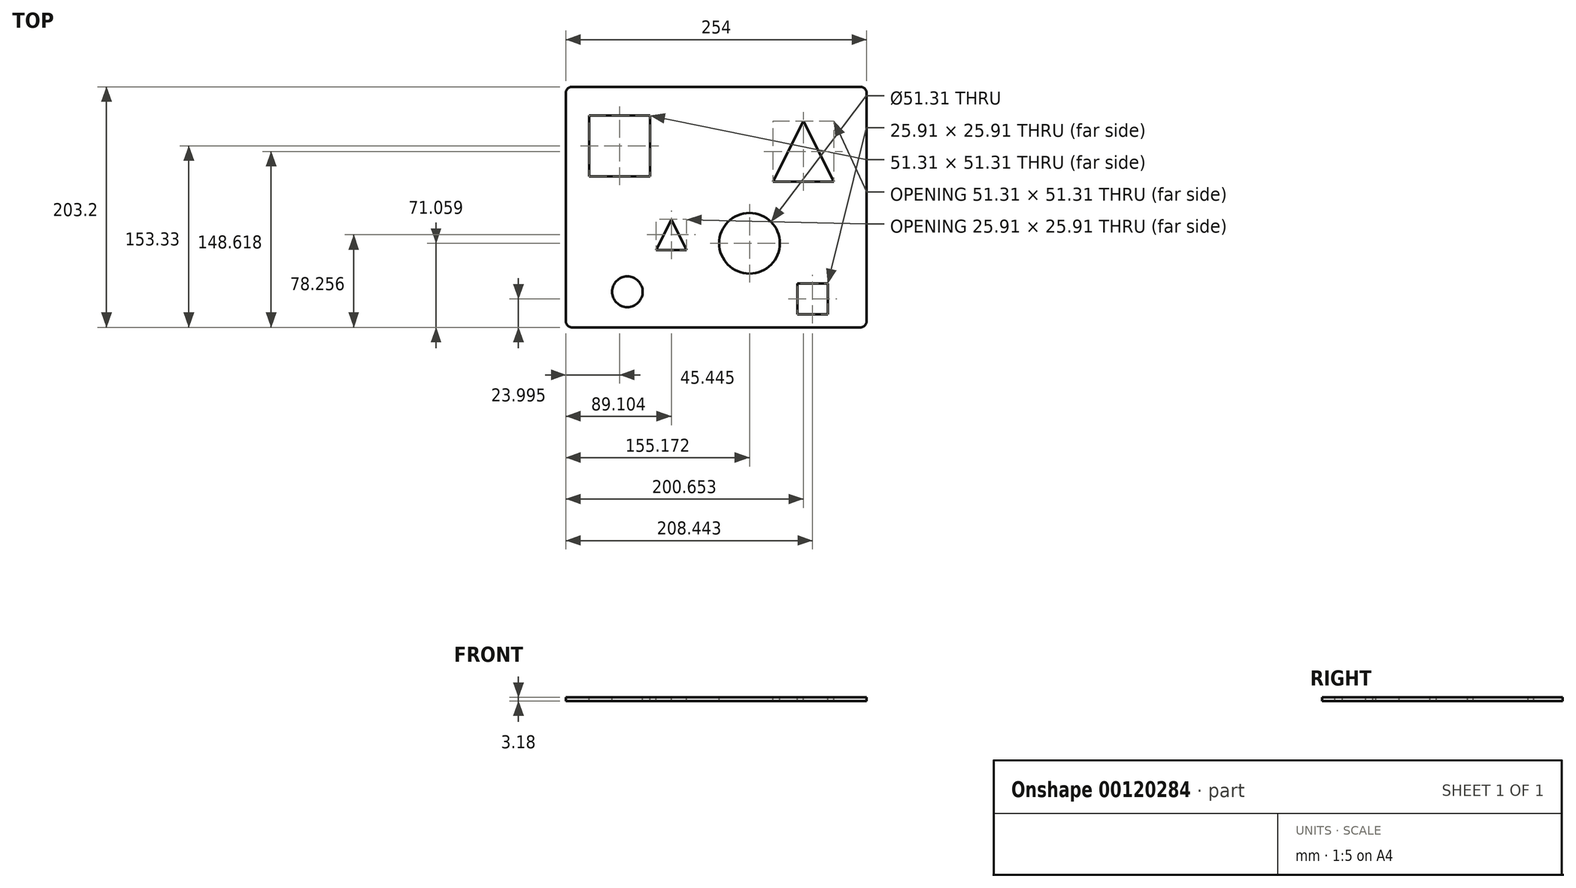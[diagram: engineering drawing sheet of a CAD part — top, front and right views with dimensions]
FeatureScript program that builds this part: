
annotation { "Feature Type Name" : "Feature", "Feature Type Description" : "" }
export const myFeature = defineFeature(function(context is Context, id is Id, definition is map)
    precondition{}
    {
        {
            var Q0;
            Q0=qCreatedBy(makeId("Top.planeOp"),FACE);
            var sketch = newSketch(context, id + "F0", { "sketchPlane" : qUnion([Q0])});
            skLineSegment(sketch, "E0.bottom", {"start": v(-123.95, 112) * mm, "end": v(130.05, 112) * mm});
            skLineSegment(sketch, "E0.top", {"start": v(-123.95, -91.2) * mm, "end": v(130.05, -91.2) * mm});
            skLineSegment(sketch, "E0.left", {"start": v(-123.95, 112) * mm, "end": v(-123.95, -91.2) * mm});
            skLineSegment(sketch, "E0.right", {"start": v(130.05, 112) * mm, "end": v(130.05, -91.2) * mm});
            skSolve(sketch);
        }
        {
            var Q0;
            Q0 = qSketchRegion(id + "F0", true);
            extrude(context, id + "F1", {"entities" : qUnion([Q0]), "depth" : 3.17 * mm});
        }
        {
            var Q0;
            Q0=makeQuery(id+"F1.opExtrude","CAP_FACE",FACE,{"disambiguationData":[OSD([sQuery(id+"F0.wireOp",EDGE,"E0.bottom"),sQuery(id+"F0.wireOp",EDGE,"E0.top"),sQuery(id+"F0.wireOp",EDGE,"E0.left"),sQuery(id+"F0.wireOp",EDGE,"E0.right")])],"isStart":false});
            var sketch = newSketch(context, id + "F2", { "sketchPlane" : qUnion([Q0])});
            skLineSegment(sketch, "E1.bottom", {"start": v(-104.16, 87.77) * mm, "end": v(-52.85, 87.77) * mm});
            skLineSegment(sketch, "E1.top", {"start": v(-104.16, 36.47) * mm, "end": v(-52.85, 36.47) * mm});
            skLineSegment(sketch, "E1.left", {"start": v(-104.16, 87.77) * mm, "end": v(-104.16, 36.47) * mm});
            skLineSegment(sketch, "E1.right", {"start": v(-52.85, 87.77) * mm, "end": v(-52.85, 36.47) * mm});
            skSolve(sketch);
        }
        {
            var Q0;
            Q0 = qSketchRegion(id + "F2", true);
            extrude(context, id + "F3", {"entities" : qUnion([Q0]), "operationType" : NewBodyOperationType.REMOVE, "endBound" : BoundingType.UP_TO_NEXT, "oppositeDirection" : true, "depth" : 6.35 * mm});
        }
        {
            var Q0;
            Q0=makeQuery(id+"F1.opExtrude","CAP_FACE",FACE,{"disambiguationData":[OSD([sQuery(id+"F0.wireOp",EDGE,"E0.bottom"),sQuery(id+"F0.wireOp",EDGE,"E0.top"),sQuery(id+"F0.wireOp",EDGE,"E0.left"),sQuery(id+"F0.wireOp",EDGE,"E0.right")])],"isStart":false});
            var sketch = newSketch(context, id + "F4", { "sketchPlane" : qUnion([Q0])});
            skLineSegment(sketch, "E2.bottom", {"start": v(71.54, -54.26) * mm, "end": v(97.45, -54.26) * mm});
            skLineSegment(sketch, "E2.top", {"start": v(71.54, -80.17) * mm, "end": v(97.45, -80.17) * mm});
            skLineSegment(sketch, "E2.left", {"start": v(71.54, -54.26) * mm, "end": v(71.54, -80.17) * mm});
            skLineSegment(sketch, "E2.right", {"start": v(97.45, -54.26) * mm, "end": v(97.45, -80.17) * mm});
            skSolve(sketch);
        }
        {
            var Q0;
            Q0 = qSketchRegion(id + "F4", true);
            extrude(context, id + "F5", {"entities" : qUnion([Q0]), "operationType" : NewBodyOperationType.REMOVE, "endBound" : BoundingType.UP_TO_NEXT, "oppositeDirection" : true, "depth" : 6.35 * mm});
        }
        {
            var Q0;
            Q0=makeQuery(id+"F1.opExtrude","CAP_FACE",FACE,{"disambiguationData":[OSD([sQuery(id+"F0.wireOp",EDGE,"E0.bottom"),sQuery(id+"F0.wireOp",EDGE,"E0.top"),sQuery(id+"F0.wireOp",EDGE,"E0.left"),sQuery(id+"F0.wireOp",EDGE,"E0.right")])],"isStart":false});
            var sketch = newSketch(context, id + "F6", { "sketchPlane" : qUnion([Q0])});
            skCircle(sketch, "E3", {"center": v(-71.98, -61.13) * mm, "radius": 12.95 * mm});
            skSolve(sketch);
        }
        {
            var Q0;
            Q0 = qSketchRegion(id + "F6", true);
            extrude(context, id + "F7", {"entities" : qUnion([Q0]), "operationType" : NewBodyOperationType.REMOVE, "endBound" : BoundingType.UP_TO_NEXT, "oppositeDirection" : true, "depth" : 6.35 * mm});
        }
        {
            var Q0;
            Q0=makeQuery(id+"F1.opExtrude","CAP_FACE",FACE,{"disambiguationData":[OSD([sQuery(id+"F0.wireOp",EDGE,"E0.bottom"),sQuery(id+"F0.wireOp",EDGE,"E0.top"),sQuery(id+"F0.wireOp",EDGE,"E0.left"),sQuery(id+"F0.wireOp",EDGE,"E0.right")])],"isStart":false});
            var sketch = newSketch(context, id + "F8", { "sketchPlane" : qUnion([Q0])});
            skLineSegment(sketch, "E4", {"start": v(51.05, 31.75) * mm, "end": v(102.36, 31.75) * mm});
            skLineSegment(sketch, "E5", {"start": v(76.7, 31.75) * mm, "end": v(76.7, 83.06) * mm, "construction": true});
            skLineSegment(sketch, "E6", {"start": v(51.05, 31.75) * mm, "end": v(76.7, 83.06) * mm});
            skLineSegment(sketch, "E7", {"start": v(76.7, 83.06) * mm, "end": v(102.36, 31.75) * mm});
            skSolve(sketch);
        }
        {
            var Q0;
            Q0 = qSketchRegion(id + "F8", true);
            extrude(context, id + "F9", {"entities" : qUnion([Q0]), "operationType" : NewBodyOperationType.REMOVE, "endBound" : BoundingType.THROUGH_ALL, "oppositeDirection" : true, "depth" : 6.35 * mm});
        }
        {
            var Q0;
            Q0=makeQuery(id+"F1.opExtrude","CAP_FACE",FACE,{"disambiguationData":[OSD([sQuery(id+"F0.wireOp",EDGE,"E0.bottom"),sQuery(id+"F0.wireOp",EDGE,"E0.top"),sQuery(id+"F0.wireOp",EDGE,"E0.left"),sQuery(id+"F0.wireOp",EDGE,"E0.right")])],"isStart":false});
            var sketch = newSketch(context, id + "F10", { "sketchPlane" : qUnion([Q0])});
            skCircle(sketch, "E8", {"center": v(31.22, -20.15) * mm, "radius": 25.65 * mm});
            skSolve(sketch);
        }
        {
            var Q0;
            Q0 = qSketchRegion(id + "F10", true);
            extrude(context, id + "F11", {"entities" : qUnion([Q0]), "operationType" : NewBodyOperationType.REMOVE, "endBound" : BoundingType.UP_TO_NEXT, "oppositeDirection" : true, "depth" : 6.35 * mm});
        }
        {
            var Q0;
            Q0=makeQuery(id+"F1.opExtrude","CAP_FACE",FACE,{"disambiguationData":[OSD([sQuery(id+"F0.wireOp",EDGE,"E0.bottom"),sQuery(id+"F0.wireOp",EDGE,"E0.top"),sQuery(id+"F0.wireOp",EDGE,"E0.left"),sQuery(id+"F0.wireOp",EDGE,"E0.right")])],"isStart":false});
            var sketch = newSketch(context, id + "F12", { "sketchPlane" : qUnion([Q0])});
            skLineSegment(sketch, "E9", {"start": v(-47.8, -25.9) * mm, "end": v(-21.9, -25.9) * mm});
            skLineSegment(sketch, "E10", {"start": v(-34.85, -25.9) * mm, "end": v(-34.85, 0) * mm, "construction": true});
            skLineSegment(sketch, "E11", {"start": v(-47.8, -25.9) * mm, "end": v(-34.85, 0) * mm});
            skLineSegment(sketch, "E12", {"start": v(-21.9, -25.9) * mm, "end": v(-34.85, 0) * mm});
            skSolve(sketch);
        }
        {
            var Q0;
            Q0 = qSketchRegion(id + "F12", true);
            extrude(context, id + "F13", {"entities" : qUnion([Q0]), "operationType" : NewBodyOperationType.REMOVE, "endBound" : BoundingType.UP_TO_NEXT, "oppositeDirection" : true, "depth" : 6.35 * mm});
        }
        {
            var Q0;
            Q0=makeQuery(id+"F1.opExtrude","SWEPT_EDGE",EDGE,{"disambiguationData":[OSD([sQuery(id+"F0.wireOp",EDGE,"E0.bottom"),sQuery(id+"F0.wireOp",EDGE,"E0.left")])]});
            fillet(context, id + "F14", {"entities" : qUnion([Q0]), "radius" : 5.08 * mm, "tangentPropagation" : true, "allowEdgeOverflow" : false});
        }
        {
            var Q0;
            Q0=makeQuery(id+"F1.opExtrude","SWEPT_EDGE",EDGE,{"disambiguationData":[OSD([sQuery(id+"F0.wireOp",EDGE,"E0.bottom"),sQuery(id+"F0.wireOp",EDGE,"E0.right")])]});
            fillet(context, id + "F15", {"entities" : qUnion([Q0]), "radius" : 5.08 * mm, "tangentPropagation" : true, "allowEdgeOverflow" : false});
        }
        {
            var Q0;
            Q0=makeQuery(id+"F1.opExtrude","SWEPT_EDGE",EDGE,{"disambiguationData":[OSD([sQuery(id+"F0.wireOp",EDGE,"E0.top"),sQuery(id+"F0.wireOp",EDGE,"E0.right")])]});
            fillet(context, id + "F16", {"entities" : qUnion([Q0]), "radius" : 5.08 * mm, "tangentPropagation" : true, "allowEdgeOverflow" : false});
        }
        {
            var Q0;
            Q0=makeQuery(id+"F1.opExtrude","SWEPT_EDGE",EDGE,{"disambiguationData":[OSD([sQuery(id+"F0.wireOp",EDGE,"E0.top"),sQuery(id+"F0.wireOp",EDGE,"E0.left")])]});
            fillet(context, id + "F17", {"entities" : qUnion([Q0]), "radius" : 5.08 * mm, "tangentPropagation" : true, "allowEdgeOverflow" : false});
        }
    });
